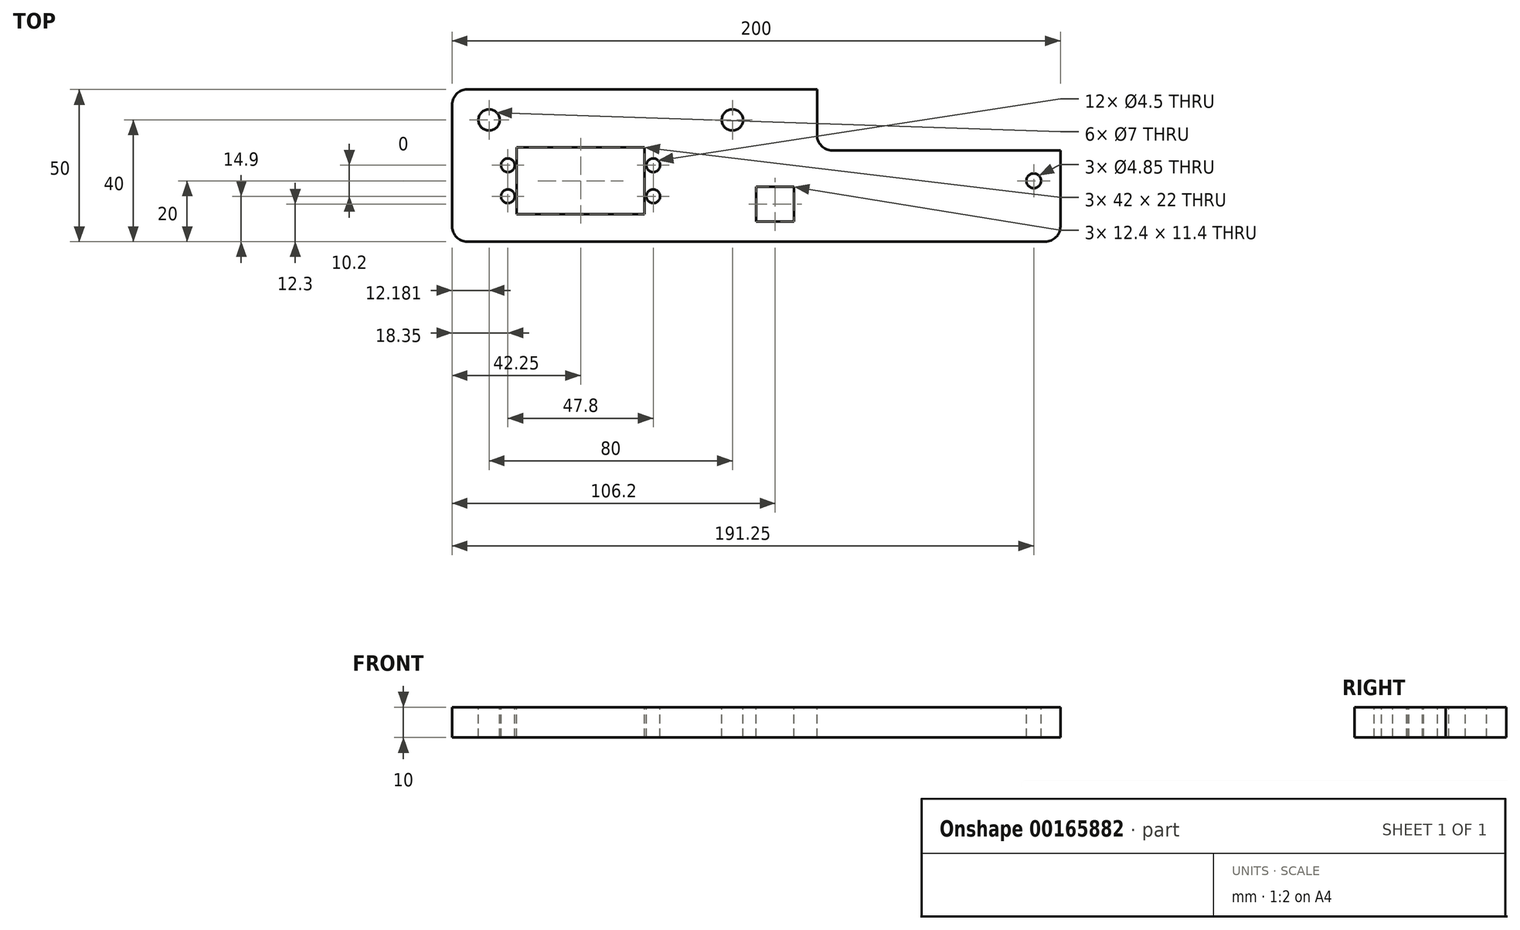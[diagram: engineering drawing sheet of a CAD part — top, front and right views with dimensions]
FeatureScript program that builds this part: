
annotation { "Feature Type Name" : "Feature", "Feature Type Description" : "" }
export const myFeature = defineFeature(function(context is Context, id is Id, definition is map)
    precondition{}
    {
        {
            var Q0;
            Q0=qCreatedBy(makeId("Top.planeOp"),FACE);
            var sketch = newSketch(context, id + "F0", { "sketchPlane" : qUnion([Q0])});
            skLineSegment(sketch, "E0.bottom", {"start": v(100, -25) * mm, "end": v(-100, -25) * mm});
            skLineSegment(sketch, "E0.top", {"start": v(100, 25) * mm, "end": v(-100, 25) * mm});
            skLineSegment(sketch, "E0.left", {"start": v(100, -25) * mm, "end": v(100, 25) * mm});
            skLineSegment(sketch, "E0.right", {"start": v(-100, -25) * mm, "end": v(-100, 25) * mm});
            skPoint(sketch, "E0.middle", {"position": v(0, 0) * mm});
            skSolve(sketch);
        }
        {
            var Q0;
            Q0=makeQuery(id+"F0.imprint","IMPRINT",FACE,{"disambiguationData":[TD([[makeQuery(id+"F0.imprint","IMPRINT",EDGE,{"derivedFrom":sQuery(id+"F0.wireOp",EDGE,"E0.bottom")}),-1.0]])]});
            extrude(context, id + "F1", {"entities" : qUnion([Q0]), "depth" : 10 * mm});
        }
        {
            var Q0;
            Q0=makeQuery(id+"F1.opExtrude","CAP_FACE",FACE,{"disambiguationData":[OSD([sQuery(id+"F0.wireOp",EDGE,"E0.bottom"),sQuery(id+"F0.wireOp",EDGE,"E0.top"),sQuery(id+"F0.wireOp",EDGE,"E0.left"),sQuery(id+"F0.wireOp",EDGE,"E0.right")])],"isStart":false});
            var sketch = newSketch(context, id + "F2", { "sketchPlane" : qUnion([Q0])});
            skLineSegment(sketch, "E1.bottom", {"start": v(-78.75, -16) * mm, "end": v(-36.75, -16) * mm});
            skLineSegment(sketch, "E1.top", {"start": v(-78.75, 6) * mm, "end": v(-36.75, 6) * mm});
            skLineSegment(sketch, "E1.left", {"start": v(-78.75, -16) * mm, "end": v(-78.75, 6) * mm});
            skLineSegment(sketch, "E1.right", {"start": v(-36.75, -16) * mm, "end": v(-36.75, 6) * mm});
            skPoint(sketch, "E1.middle", {"position": v(-57.75, -5) * mm});
            skSolve(sketch);
        }
        {
            var Q0;
            Q0=makeQuery(id+"F2.imprint","IMPRINT",FACE,{"disambiguationData":[TD([[makeQuery(id+"F2.imprint","IMPRINT",EDGE,{"derivedFrom":sQuery(id+"F2.wireOp",EDGE,"E1.bottom")}),1.0]])]});
            extrude(context, id + "F3", {"entities" : qUnion([Q0]), "operationType" : NewBodyOperationType.REMOVE, "endBound" : BoundingType.THROUGH_ALL, "oppositeDirection" : true, "depth" : 25 * mm});
        }
        {
            var Q0;
            Q0=makeQuery(id+"F1.opExtrude","CAP_FACE",FACE,{"disambiguationData":[OSD([sQuery(id+"F0.wireOp",EDGE,"E0.bottom"),sQuery(id+"F0.wireOp",EDGE,"E0.top"),sQuery(id+"F0.wireOp",EDGE,"E0.left"),sQuery(id+"F0.wireOp",EDGE,"E0.right")])],"isStart":false});
            var sketch = newSketch(context, id + "F4", { "sketchPlane" : qUnion([Q0])});
            skLineSegment(sketch, "E2.bottom", {"start": v(-81.65, 0.1) * mm, "end": v(-33.85, 0.1) * mm});
            skLineSegment(sketch, "E2.top", {"start": v(-81.65, -10.1) * mm, "end": v(-33.85, -10.1) * mm});
            skLineSegment(sketch, "E2.left", {"start": v(-81.65, 0.1) * mm, "end": v(-81.65, -10.1) * mm});
            skLineSegment(sketch, "E2.right", {"start": v(-33.85, 0.1) * mm, "end": v(-33.85, -10.1) * mm});
            skPoint(sketch, "E2.middle", {"position": v(-57.75, -5) * mm});
            skPoint(sketch, "E2.middle.positionSnap0", {"position": v(-78.75, -5) * mm});
            skPoint(sketch, "E2.middle.positionSnap1", {"position": v(-57.75, -16) * mm});
            skPoint(sketch, "E2.centerSnap0", {"position": v(-78.75, -5) * mm});
            skPoint(sketch, "E2.centerSnap1", {"position": v(-57.75, -16) * mm});
            skCircle(sketch, "E3", {"center": v(-81.65, 0.1) * mm, "radius": 2.25 * mm});
            skCircle(sketch, "E4", {"center": v(-81.65, -10.1) * mm, "radius": 2.25 * mm});
            skCircle(sketch, "E5", {"center": v(-33.85, 0.1) * mm, "radius": 2.25 * mm});
            skCircle(sketch, "E6", {"center": v(-33.85, -10.1) * mm, "radius": 2.25 * mm});
            skSolve(sketch);
        }
        {
            var Q0;
            {var subQ0=sQuery(id+"F4.wireOp",EDGE,"E2.left");var subQ1=sQuery(id+"F4.wireOp",EDGE,"E2.bottom");var subQ2=makeQuery(id+"F4.imprint","INTERSECT",VERTEX,{"derivedFrom":[subQ1,subQ0]});Q0=makeQuery(id+"F4.imprint","IMPRINT",FACE,{"disambiguationData":[TD([[makeQuery(id+"F4.imprint","IMPRINT",EDGE,{"disambiguationData":[TD([[subQ2,-1.0]])],"derivedFrom":subQ1}),1.0]])]});}
            var Q1;
            {var subQ0=sQuery(id+"F4.wireOp",EDGE,"E2.left");var subQ1=sQuery(id+"F4.wireOp",EDGE,"E2.bottom");var subQ2=makeQuery(id+"F4.imprint","INTERSECT",VERTEX,{"derivedFrom":[subQ1,subQ0]});Q1=makeQuery(id+"F4.imprint","IMPRINT",FACE,{"disambiguationData":[TD([[makeQuery(id+"F4.imprint","IMPRINT",EDGE,{"disambiguationData":[TD([[subQ2,-1.0]])],"derivedFrom":subQ1}),-1.0]])]});}
            var Q2;
            {var subQ0=sQuery(id+"F4.wireOp",EDGE,"E2.left");var subQ1=sQuery(id+"F4.wireOp",EDGE,"E2.top");var subQ2=makeQuery(id+"F4.imprint","INTERSECT",VERTEX,{"derivedFrom":[subQ1,subQ0]});Q2=makeQuery(id+"F4.imprint","IMPRINT",FACE,{"disambiguationData":[TD([[makeQuery(id+"F4.imprint","IMPRINT",EDGE,{"disambiguationData":[TD([[subQ2,-1.0]])],"derivedFrom":subQ1}),-1.0]])]});}
            var Q3;
            {var subQ0=sQuery(id+"F4.wireOp",EDGE,"E2.left");var subQ1=sQuery(id+"F4.wireOp",EDGE,"E2.top");var subQ2=makeQuery(id+"F4.imprint","INTERSECT",VERTEX,{"derivedFrom":[subQ1,subQ0]});Q3=makeQuery(id+"F4.imprint","IMPRINT",FACE,{"disambiguationData":[TD([[makeQuery(id+"F4.imprint","IMPRINT",EDGE,{"disambiguationData":[TD([[subQ2,-1.0]])],"derivedFrom":subQ1}),1.0]])]});}
            var Q4;
            {var subQ0=sQuery(id+"F4.wireOp",EDGE,"E2.right");var subQ1=sQuery(id+"F4.wireOp",EDGE,"E2.bottom");var subQ2=makeQuery(id+"F4.imprint","INTERSECT",VERTEX,{"derivedFrom":[subQ1,subQ0]});Q4=makeQuery(id+"F4.imprint","IMPRINT",FACE,{"disambiguationData":[TD([[makeQuery(id+"F4.imprint","IMPRINT",EDGE,{"disambiguationData":[TD([[subQ2,1.0]])],"derivedFrom":subQ1}),-1.0]])]});}
            var Q5;
            {var subQ0=sQuery(id+"F4.wireOp",EDGE,"E2.right");var subQ1=sQuery(id+"F4.wireOp",EDGE,"E2.bottom");var subQ2=makeQuery(id+"F4.imprint","INTERSECT",VERTEX,{"derivedFrom":[subQ1,subQ0]});Q5=makeQuery(id+"F4.imprint","IMPRINT",FACE,{"disambiguationData":[TD([[makeQuery(id+"F4.imprint","IMPRINT",EDGE,{"disambiguationData":[TD([[subQ2,1.0]])],"derivedFrom":subQ1}),1.0]])]});}
            var Q6;
            {var subQ0=sQuery(id+"F4.wireOp",EDGE,"E2.right");var subQ1=sQuery(id+"F4.wireOp",EDGE,"E2.top");var subQ2=makeQuery(id+"F4.imprint","INTERSECT",VERTEX,{"derivedFrom":[subQ1,subQ0]});Q6=makeQuery(id+"F4.imprint","IMPRINT",FACE,{"disambiguationData":[TD([[makeQuery(id+"F4.imprint","IMPRINT",EDGE,{"disambiguationData":[TD([[subQ2,1.0]])],"derivedFrom":subQ1}),1.0]])]});}
            var Q7;
            {var subQ0=sQuery(id+"F4.wireOp",EDGE,"E2.right");var subQ1=sQuery(id+"F4.wireOp",EDGE,"E2.top");var subQ2=makeQuery(id+"F4.imprint","INTERSECT",VERTEX,{"derivedFrom":[subQ1,subQ0]});Q7=makeQuery(id+"F4.imprint","IMPRINT",FACE,{"disambiguationData":[TD([[makeQuery(id+"F4.imprint","IMPRINT",EDGE,{"disambiguationData":[TD([[subQ2,1.0]])],"derivedFrom":subQ1}),-1.0]])]});}
            extrude(context, id + "F5", {"entities" : qUnion([Q0, Q1, Q2, Q3, Q4, Q5, Q6, Q7]), "operationType" : NewBodyOperationType.REMOVE, "endBound" : BoundingType.THROUGH_ALL, "oppositeDirection" : true, "depth" : 25 * mm});
        }
        {
            var Q0;
            Q0=makeQuery(id+"F1.opExtrude","CAP_FACE",FACE,{"disambiguationData":[OSD([sQuery(id+"F0.wireOp",EDGE,"E0.bottom"),sQuery(id+"F0.wireOp",EDGE,"E0.top"),sQuery(id+"F0.wireOp",EDGE,"E0.left"),sQuery(id+"F0.wireOp",EDGE,"E0.right")])],"isStart":false});
            var sketch = newSketch(context, id + "F6", { "sketchPlane" : qUnion([Q0])});
            skLineSegment(sketch, "E7.bottom", {"start": v(-87.82, 15) * mm, "end": v(-7.82, 15) * mm});
            skLineSegment(sketch, "E7.top", {"start": v(-87.82, -25) * mm, "end": v(-7.82, -25) * mm});
            skLineSegment(sketch, "E7.left", {"start": v(-87.82, 15) * mm, "end": v(-87.82, -25) * mm});
            skLineSegment(sketch, "E7.right", {"start": v(-7.82, 15) * mm, "end": v(-7.82, -25) * mm});
            skCircle(sketch, "E8", {"center": v(-87.82, 15) * mm, "radius": 3.5 * mm});
            skCircle(sketch, "E9", {"center": v(-7.82, 15) * mm, "radius": 3.5 * mm});
            skSolve(sketch);
        }
        {
            var Q0;
            {var subQ0=sQuery(id+"F6.wireOp",EDGE,"E7.left");var subQ1=sQuery(id+"F6.wireOp",EDGE,"E7.bottom");var subQ2=makeQuery(id+"F6.imprint","INTERSECT",VERTEX,{"derivedFrom":[subQ1,subQ0]});Q0=makeQuery(id+"F6.imprint","IMPRINT",FACE,{"disambiguationData":[TD([[makeQuery(id+"F6.imprint","IMPRINT",EDGE,{"disambiguationData":[TD([[subQ2,-1.0]])],"derivedFrom":subQ1}),1.0]])]});}
            var Q1;
            {var subQ0=sQuery(id+"F6.wireOp",EDGE,"E7.left");var subQ1=sQuery(id+"F6.wireOp",EDGE,"E7.bottom");var subQ2=makeQuery(id+"F6.imprint","INTERSECT",VERTEX,{"derivedFrom":[subQ1,subQ0]});Q1=makeQuery(id+"F6.imprint","IMPRINT",FACE,{"disambiguationData":[TD([[makeQuery(id+"F6.imprint","IMPRINT",EDGE,{"disambiguationData":[TD([[subQ2,-1.0]])],"derivedFrom":subQ1}),-1.0]])]});}
            var Q2;
            {var subQ0=sQuery(id+"F6.wireOp",EDGE,"E7.right");var subQ1=sQuery(id+"F6.wireOp",EDGE,"E7.bottom");var subQ2=makeQuery(id+"F6.imprint","INTERSECT",VERTEX,{"derivedFrom":[subQ1,subQ0]});Q2=makeQuery(id+"F6.imprint","IMPRINT",FACE,{"disambiguationData":[TD([[makeQuery(id+"F6.imprint","IMPRINT",EDGE,{"disambiguationData":[TD([[subQ2,1.0]])],"derivedFrom":subQ1}),-1.0]])]});}
            var Q3;
            {var subQ0=sQuery(id+"F6.wireOp",EDGE,"E7.right");var subQ1=sQuery(id+"F6.wireOp",EDGE,"E7.bottom");var subQ2=makeQuery(id+"F6.imprint","INTERSECT",VERTEX,{"derivedFrom":[subQ1,subQ0]});Q3=makeQuery(id+"F6.imprint","IMPRINT",FACE,{"disambiguationData":[TD([[makeQuery(id+"F6.imprint","IMPRINT",EDGE,{"disambiguationData":[TD([[subQ2,1.0]])],"derivedFrom":subQ1}),1.0]])]});}
            extrude(context, id + "F7", {"entities" : qUnion([Q0, Q1, Q2, Q3]), "operationType" : NewBodyOperationType.REMOVE, "endBound" : BoundingType.THROUGH_ALL, "oppositeDirection" : true, "depth" : 25 * mm});
        }
        {
            var Q0;
            Q0=makeQuery(id+"F1.opExtrude","SWEPT_EDGE",EDGE,{"disambiguationData":[OSD([sQuery(id+"F0.wireOp",EDGE,"E0.top"),sQuery(id+"F0.wireOp",EDGE,"E0.right")])]});
            var Q1;
            Q1=makeQuery(id+"F1.opExtrude","SWEPT_EDGE",EDGE,{"disambiguationData":[OSD([sQuery(id+"F0.wireOp",EDGE,"E0.bottom"),sQuery(id+"F0.wireOp",EDGE,"E0.right")])]});
            var Q2;
            Q2=makeQuery(id+"F1.opExtrude","SWEPT_EDGE",EDGE,{"disambiguationData":[OSD([sQuery(id+"F0.wireOp",EDGE,"E0.top"),sQuery(id+"F0.wireOp",EDGE,"E0.left")])]});
            var Q3;
            Q3=makeQuery(id+"F1.opExtrude","SWEPT_EDGE",EDGE,{"disambiguationData":[OSD([sQuery(id+"F0.wireOp",EDGE,"E0.bottom"),sQuery(id+"F0.wireOp",EDGE,"E0.left")])]});
            fillet(context, id + "F8", {"entities" : qUnion([Q0, Q1, Q2, Q3]), "radius" : 5 * mm, "tangentPropagation" : true, "allowEdgeOverflow" : false});
        }
        {
            var Q0;
            Q0=makeQuery(id+"F1.opExtrude","CAP_FACE",FACE,{"disambiguationData":[OSD([sQuery(id+"F0.wireOp",EDGE,"E0.bottom"),sQuery(id+"F0.wireOp",EDGE,"E0.top"),sQuery(id+"F0.wireOp",EDGE,"E0.left"),sQuery(id+"F0.wireOp",EDGE,"E0.right")])],"isStart":false});
            var sketch = newSketch(context, id + "F9", { "sketchPlane" : qUnion([Q0])});
            skLineSegment(sketch, "E10.bottom", {"start": v(0, -7) * mm, "end": v(12.4, -7) * mm});
            skLineSegment(sketch, "E10.top", {"start": v(0, -18.4) * mm, "end": v(12.4, -18.4) * mm});
            skLineSegment(sketch, "E10.left", {"start": v(0, -7) * mm, "end": v(0, -18.4) * mm});
            skLineSegment(sketch, "E10.right", {"start": v(12.4, -7) * mm, "end": v(12.4, -18.4) * mm});
            skSolve(sketch);
        }
        {
            var Q0;
            Q0=makeQuery(id+"F1.opExtrude","CAP_FACE",FACE,{"disambiguationData":[OSD([sQuery(id+"F0.wireOp",EDGE,"E0.bottom"),sQuery(id+"F0.wireOp",EDGE,"E0.top"),sQuery(id+"F0.wireOp",EDGE,"E0.left"),sQuery(id+"F0.wireOp",EDGE,"E0.right")])],"isStart":false});
            var sketch = newSketch(context, id + "F10", { "sketchPlane" : qUnion([Q0])});
            skLineSegment(sketch, "E11.bottom", {"start": v(-78.75, -5) * mm, "end": v(91.25, -5) * mm});
            skLineSegment(sketch, "E11.top", {"start": v(-78.75, -25) * mm, "end": v(91.25, -25) * mm});
            skLineSegment(sketch, "E11.left", {"start": v(-78.75, -5) * mm, "end": v(-78.75, -25) * mm});
            skLineSegment(sketch, "E11.right", {"start": v(91.25, -5) * mm, "end": v(91.25, -25) * mm});
            skCircle(sketch, "E12", {"center": v(91.25, -5) * mm, "radius": 2.43 * mm});
            skSolve(sketch);
        }
        {
            var Q0;
            {var subQ0=sQuery(id+"F10.wireOp",EDGE,"E11.right");Q0=makeQuery(id+"F10.imprint","IMPRINT",FACE,{"disambiguationData":[TD([[makeQuery(id+"F10.imprint","IMPRINT",EDGE,{"derivedFrom":subQ0}),1.0]])]});}
            var sketch = newSketch(context, id + "F11", { "sketchPlane" : qUnion([Q0])});
            skLineSegment(sketch, "E13.bottom", {"start": v(100, 5) * mm, "end": v(20, 5) * mm});
            skLineSegment(sketch, "E13.top", {"start": v(100, 25) * mm, "end": v(20, 25) * mm});
            skLineSegment(sketch, "E13.left", {"start": v(100, 5) * mm, "end": v(100, 25) * mm});
            skLineSegment(sketch, "E13.right", {"start": v(20, 5) * mm, "end": v(20, 25) * mm});
            skSolve(sketch);
        }
        {
            var Q0;
            Q0 = qSketchRegion(id + "F11", true);
            var Q1;
            {var subQ0=sQuery(id+"F10.wireOp",EDGE,"E11.right");var subQ1=sQuery(id+"F10.wireOp",EDGE,"E11.bottom");var subQ2=makeQuery(id+"F10.imprint","INTERSECT",VERTEX,{"derivedFrom":[subQ1,subQ0]});Q1=makeQuery(id+"F10.imprint","IMPRINT",FACE,{"disambiguationData":[TD([[makeQuery(id+"F10.imprint","IMPRINT",EDGE,{"disambiguationData":[TD([[subQ2,1.0]])],"derivedFrom":subQ1}),1.0]])]});}
            var Q2;
            {var subQ0=sQuery(id+"F10.wireOp",EDGE,"E11.right");var subQ1=sQuery(id+"F10.wireOp",EDGE,"E11.bottom");var subQ2=makeQuery(id+"F10.imprint","INTERSECT",VERTEX,{"derivedFrom":[subQ1,subQ0]});Q2=makeQuery(id+"F10.imprint","IMPRINT",FACE,{"disambiguationData":[TD([[makeQuery(id+"F10.imprint","IMPRINT",EDGE,{"disambiguationData":[TD([[subQ2,1.0]])],"derivedFrom":subQ1}),-1.0]])]});}
            var Q3;
            Q3=makeQuery(id+"F9.imprint","IMPRINT",FACE,{"disambiguationData":[TD([[makeQuery(id+"F9.imprint","IMPRINT",EDGE,{"derivedFrom":sQuery(id+"F9.wireOp",EDGE,"E10.bottom")}),-1.0]])]});
            extrude(context, id + "F12", {"entities" : qUnion([Q0, Q1, Q2, Q3]), "operationType" : NewBodyOperationType.REMOVE, "endBound" : BoundingType.THROUGH_ALL, "oppositeDirection" : true, "depth" : 25 * mm});
        }
        {
            var Q0;
            Q0=makeQuery(id+"F12.boolean.opBoolean","COPY",EDGE,{"derivedFrom":makeQuery(id+"F12.opExtrude","SWEPT_EDGE",EDGE,{"disambiguationData":[OSD([sQuery(id+"F0.wireOp",EDGE,"E0.top"),sQuery(id+"F11.wireOp",EDGE,"E13.top"),sQuery(id+"F11.wireOp",EDGE,"E13.right")])]})});
            var Q1;
            Q1=makeQuery(id+"F12.boolean.opBoolean","COPY",EDGE,{"derivedFrom":makeQuery(id+"F12.opExtrude","SWEPT_EDGE",EDGE,{"disambiguationData":[OSD([sQuery(id+"F11.wireOp",EDGE,"E13.bottom"),sQuery(id+"F11.wireOp",EDGE,"E13.right")])]})});
            var Q2;
            Q2=makeQuery(id+"F12.boolean.opBoolean","COPY",EDGE,{"derivedFrom":makeQuery(id+"F12.opExtrude","SWEPT_EDGE",EDGE,{"disambiguationData":[OSD([sQuery(id+"F0.wireOp",EDGE,"E0.left"),sQuery(id+"F11.wireOp",EDGE,"E13.bottom"),sQuery(id+"F11.wireOp",EDGE,"E13.left")])]})});
            fillet(context, id + "F13", {"entities" : qUnion([Q0, Q1, Q2]), "radius" : 5 * mm, "tangentPropagation" : true, "allowEdgeOverflow" : false});
        }
    });
